# Revit family: Robe_Hook-American_Standard-TS_Series-7455210
name_source: partatom
category: Specialty Equipment
revit_build: Autodesk Revit 2018 (Build: 20170223_1515(x64)
units: mm (PartAtom-declared; Revit-internal decimal feet)

## family parameters
Cut with Voids When Loaded = No
Host = Face
OmniClass Number = 23.40.20.21.31
OmniClass Title = Robe Hooks
Part Type = Normal
Room Calculation Point = No
Round Connector Dimension = Use Diameter
Shared = Yes

## types (4) — shared parameters
Assembly Code = C1030220
Default Elevation = 60"
Description = TS Series Bath Accessories Robe Hook
Height = 3 5/8"
Installation Type = Wall Mount
Length = 4 1/8"
Manufacturer = American Standard
Model = 7455210
Price = Prices may vary. Please consult Manufacturer Representative for most up-to-date price list.
Product Documentation Link = https://americanstandard.box.com
Product Page URL = https://www.americanstandard-us.com
Specification = Robe Hook shall feature metal construction. Shall feature concealed mounting with no exposed set screws.
URL = https://www.americanstandard-us.com
Warranty Information = 1 Year General Product Warranty
Width = 2 1/4"

## per-type parameters (varying)
| type | Finish | Material |
| 7455210.002 | Metal-American Standard-002-Polished Chrome | Metal-American Standard-002-Polished Chrome |
| 7455210.295 | Metal-American Standard-295-Brushed Nickel | Metal-American Standard-295-Brushed Nickel |
| 7455210.013 | Metal-American Standard-013-Polished Nickel | Metal-American Standard-013-Polished Nickel |
| 7455210.278 | Metal- American Standard-278-Legacy Bronze | Metal- American Standard-278-Legacy Bronze |

## geometry (parser evidence)
native form markers: Sweep x2
no freeform markers — native parametric forms only
